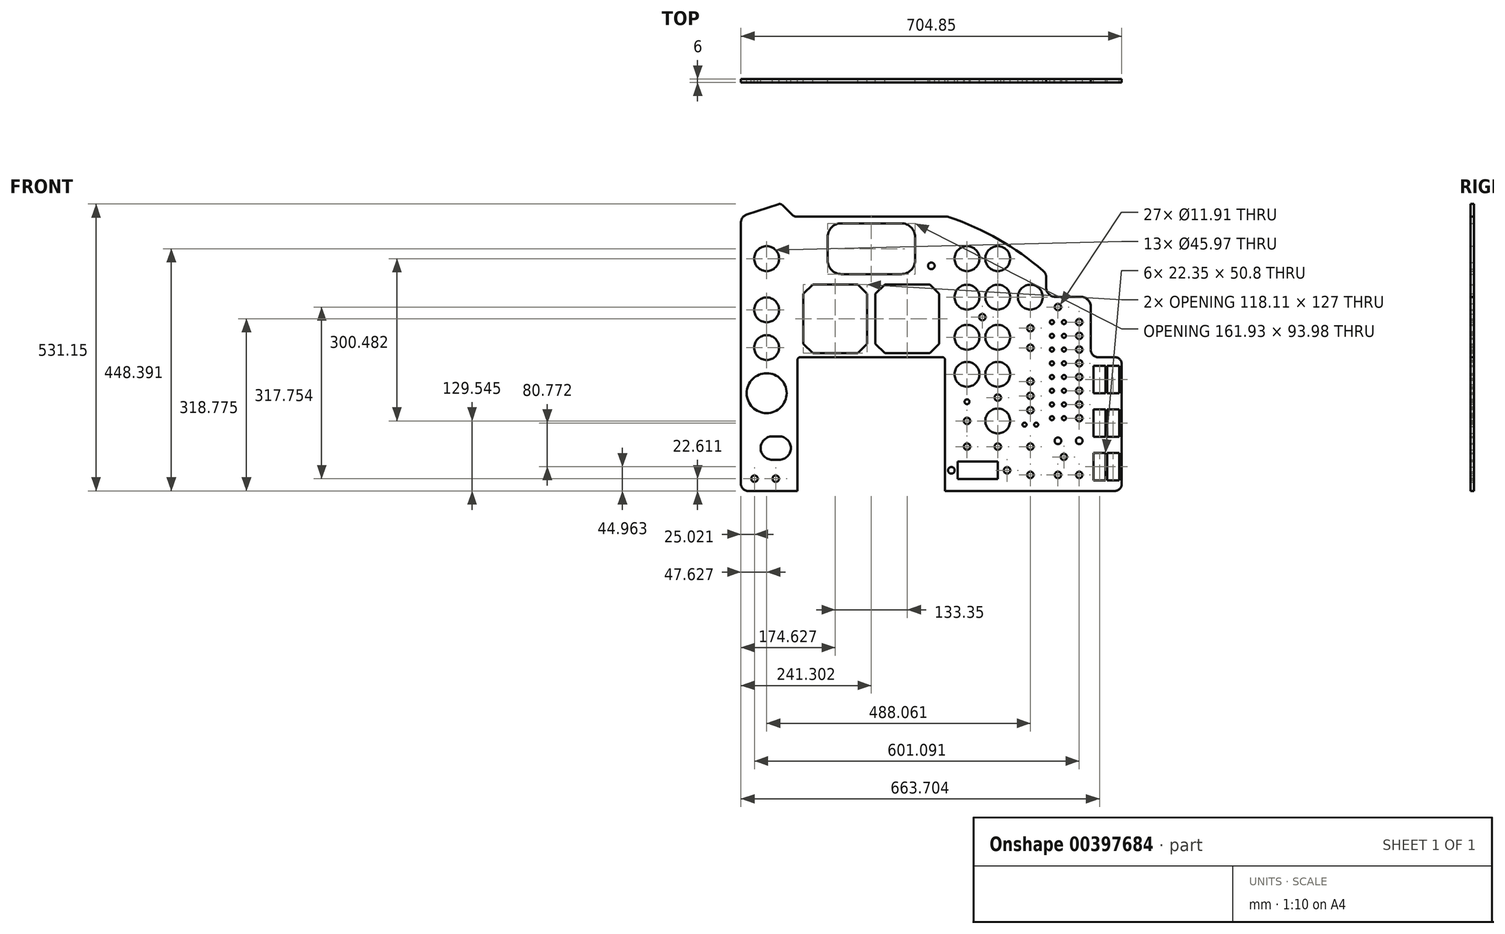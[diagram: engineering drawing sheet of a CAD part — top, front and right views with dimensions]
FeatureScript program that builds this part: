
annotation { "Feature Type Name" : "Feature", "Feature Type Description" : "" }
export const myFeature = defineFeature(function(context is Context, id is Id, definition is map)
    precondition{}
    {
        {
            var Q0;
            Q0=qCreatedBy(makeId("Front.planeOp"),FACE);
            var sketch = newSketch(context, id + "F0", { "sketchPlane" : qUnion([Q0])});
            skLineSegment(sketch, "E0", {"start": v(-241.06, -131.64) * mm, "end": v(-148.98, -131.64) * mm});
            skLineSegment(sketch, "E1", {"start": v(-148.98, -131.64) * mm, "end": v(-148.98, 110.93) * mm});
            skLineSegment(sketch, "E2", {"start": v(-143.9, 116.01) * mm, "end": v(118.99, 116.01) * mm});
            skLineSegment(sketch, "E3", {"start": v(124.07, 110.93) * mm, "end": v(124.07, -131.64) * mm});
            skLineSegment(sketch, "E4", {"start": v(124.07, -131.64) * mm, "end": v(311.4, -131.64) * mm});
            skLineSegment(sketch, "E5", {"start": v(-253.76, 255.71) * mm, "end": v(-253.76, -118.94) * mm});
            skLineSegment(sketch, "E6", {"start": v(-152.74, 376.44) * mm, "end": v(117.72, 376.44) * mm});
            skLineSegment(sketch, "E7", {"start": v(-253.76, 255.71) * mm, "end": v(-253.76, 365.39) * mm});
            skLineSegment(sketch, "E8", {"start": v(311.4, -131.64) * mm, "end": v(438.4, -131.64) * mm});
            skLineSegment(sketch, "E9", {"start": v(451.1, -118.94) * mm, "end": v(451.1, 103.31) * mm});
            skLineSegment(sketch, "E10", {"start": v(438.4, 116.01) * mm, "end": v(406.64, 116.01) * mm});
            skLineSegment(sketch, "E11", {"start": v(393.94, 128.71) * mm, "end": v(393.94, 208.72) * mm});
            skLineSegment(sketch, "E12", {"start": v(374.9, 227.77) * mm, "end": v(327.9, 227.77) * mm});
            skLineSegment(sketch, "E13", {"start": v(-243.25, 379.87) * mm, "end": v(-184.35, 399.13) * mm});
            skLineSegment(sketch, "E14", {"start": v(-157.18, 378.26) * mm, "end": v(-176.65, 397.33) * mm});
            skLineSegment(sketch, "E15", {"start": v(117.72, 376.44) * mm, "end": v(123.7, 376.44) * mm});
            skLineSegment(sketch, "E16", {"start": v(311.4, 255.71) * mm, "end": v(311.4, 263.42) * mm});
            skLineSegment(sketch, "E17", {"start": v(-253.76, 376.44) * mm, "end": v(-155.33, 376.44) * mm, "construction": true});
            skLineSegment(sketch, "E18", {"start": v(-179.95, 400.57) * mm, "end": v(-179.95, 376.44) * mm, "construction": true});
            skLineSegment(sketch, "E19", {"start": v(217.5, 323.68) * mm, "end": v(223.32, 333.8) * mm, "construction": true});
            skArc(sketch, "E20", {"start": v(305.6, 275.97) * mm, "mid": v(223.45, 333.73) * mm, "end": v(131.93, 375.07) * mm});
            skLineSegment(sketch, "E21", {"start": v(127.88, 376.44) * mm, "end": v(311.4, 270.95) * mm, "construction": true});
            skPoint(sketch, "E22.visualSharp", {"position": v(451.1, -131.64) * mm});
            skArc(sketch, "E22.filletArc", {"start": v(438.4, -131.64) * mm, "mid": v(447.37, -127.92) * mm, "end": v(451.1, -118.94) * mm});
            skPoint(sketch, "E23.visualSharp", {"position": v(451.1, 116.01) * mm});
            skArc(sketch, "E23.filletArc", {"start": v(451.1, 103.31) * mm, "mid": v(447.37, 112.3) * mm, "end": v(438.4, 116.01) * mm});
            skPoint(sketch, "E24.visualSharp", {"position": v(393.94, 116.01) * mm});
            skArc(sketch, "E24.filletArc", {"start": v(393.94, 128.71) * mm, "mid": v(397.66, 119.73) * mm, "end": v(406.64, 116.01) * mm});
            skPoint(sketch, "E25.visualSharp", {"position": v(393.94, 227.77) * mm});
            skArc(sketch, "E25.filletArc", {"start": v(393.94, 208.72) * mm, "mid": v(388.36, 222.2) * mm, "end": v(374.9, 227.77) * mm});
            skPoint(sketch, "E26.visualSharp", {"position": v(124.07, 116.01) * mm});
            skArc(sketch, "E26.filletArc", {"start": v(124.07, 110.93) * mm, "mid": v(122.58, 114.53) * mm, "end": v(118.99, 116.01) * mm});
            skPoint(sketch, "E27.visualSharp", {"position": v(-148.98, 116.01) * mm});
            skArc(sketch, "E27.filletArc", {"start": v(-143.9, 116.01) * mm, "mid": v(-147.5, 114.53) * mm, "end": v(-148.98, 110.93) * mm});
            skPoint(sketch, "E28.visualSharp", {"position": v(-253.76, -131.64) * mm});
            skArc(sketch, "E28.filletArc", {"start": v(-253.76, -118.94) * mm, "mid": v(-250.04, -127.92) * mm, "end": v(-241.06, -131.64) * mm});
            skPoint(sketch, "E29.visualSharp", {"position": v(-155.33, 376.44) * mm});
            skArc(sketch, "E29.filletArc", {"start": v(-157.18, 378.26) * mm, "mid": v(-155.14, 376.91) * mm, "end": v(-152.74, 376.44) * mm});
            skPoint(sketch, "E30.visualSharp", {"position": v(-179.95, 400.57) * mm});
            skArc(sketch, "E30.filletArc", {"start": v(-176.65, 397.33) * mm, "mid": v(-180.25, 399.31) * mm, "end": v(-184.35, 399.13) * mm});
            skPoint(sketch, "E31.visualSharp", {"position": v(-253.76, 376.44) * mm});
            skArc(sketch, "E31.filletArc", {"start": v(-243.25, 379.87) * mm, "mid": v(-250.86, 374.34) * mm, "end": v(-253.76, 365.39) * mm});
            skLineSegment(sketch, "E32", {"start": v(311.4, 255.71) * mm, "end": v(311.4, 244.28) * mm});
            skPoint(sketch, "E33.visualSharp", {"position": v(311.4, 227.77) * mm});
            skArc(sketch, "E33.filletArc", {"start": v(311.4, 244.28) * mm, "mid": v(316.23, 232.61) * mm, "end": v(327.9, 227.77) * mm});
            skPoint(sketch, "E34.visualSharp", {"position": v(311.4, 270.95) * mm});
            skArc(sketch, "E34.filletArc", {"start": v(311.4, 263.42) * mm, "mid": v(309.88, 270.33) * mm, "end": v(305.6, 275.97) * mm});
            skPoint(sketch, "E35.visualSharp", {"position": v(127.88, 376.44) * mm});
            skArc(sketch, "E35.filletArc", {"start": v(131.93, 375.07) * mm, "mid": v(127.87, 376.1) * mm, "end": v(123.7, 376.44) * mm});
            skLineSegment(sketch, "E36", {"start": v(-206.13, -131.64) * mm, "end": v(-206.13, 376.44) * mm, "construction": true});
            skCircle(sketch, "E37", {"center": v(-206.13, 49.34) * mm, "radius": 36.96 * mm});
            skCircle(sketch, "E38", {"center": v(-206.13, 133.67) * mm, "radius": 22.99 * mm});
            skCircle(sketch, "E39", {"center": v(-206.13, 203.52) * mm, "radius": 22.99 * mm});
            skCircle(sketch, "E40", {"center": v(-206.13, 298.39) * mm, "radius": 22.99 * mm});
            skLineSegment(sketch, "E41", {"start": v(164.7, -131.64) * mm, "end": v(164.7, 355.27) * mm, "construction": true});
            skLineSegment(sketch, "E42", {"start": v(221.6, -131.64) * mm, "end": v(221.6, 322.57) * mm, "construction": true});
            skLineSegment(sketch, "E43", {"start": v(281.93, -131.64) * mm, "end": v(281.93, 287.9) * mm, "construction": true});
            skCircle(sketch, "E44", {"center": v(164.7, 84.26) * mm, "radius": 22.99 * mm});
            skCircle(sketch, "E45", {"center": v(164.7, 152.84) * mm, "radius": 22.99 * mm});
            skCircle(sketch, "E46", {"center": v(221.6, 152.84) * mm, "radius": 22.99 * mm});
            skCircle(sketch, "E47", {"center": v(221.6, 84.26) * mm, "radius": 22.99 * mm});
            skCircle(sketch, "E48", {"center": v(164.7, 227.14) * mm, "radius": 22.99 * mm});
            skCircle(sketch, "E49", {"center": v(221.6, 227.14) * mm, "radius": 22.99 * mm});
            skCircle(sketch, "E50", {"center": v(164.7, 298.39) * mm, "radius": 22.99 * mm});
            skCircle(sketch, "E51", {"center": v(221.6, 298.39) * mm, "radius": 22.99 * mm});
            skCircle(sketch, "E52", {"center": v(281.93, 227.14) * mm, "radius": 22.99 * mm});
            skLineSegment(sketch, "E53", {"start": v(372.35, -131.64) * mm, "end": v(372.35, 227.77) * mm, "construction": true});
            skLineSegment(sketch, "E54", {"start": v(332.98, -131.64) * mm, "end": v(332.98, 227.77) * mm, "construction": true});
            skLineSegment(sketch, "E55", {"start": v(435.34, -131.64) * mm, "end": v(435.34, 116.01) * mm, "construction": true});
            skLineSegment(sketch, "E56", {"start": v(409.94, -131.64) * mm, "end": v(409.94, 116.01) * mm, "construction": true});
            skCircle(sketch, "E57", {"center": v(372.35, 2.98) * mm, "radius": 5.95 * mm});
            skCircle(sketch, "E58.0.1.0", {"center": v(372.35, 28.38) * mm, "radius": 5.95 * mm});
            skCircle(sketch, "E58.0.2.0", {"center": v(372.35, 53.78) * mm, "radius": 5.95 * mm});
            skCircle(sketch, "E58.0.3.0", {"center": v(372.35, 79.18) * mm, "radius": 5.95 * mm});
            skCircle(sketch, "E58.0.4.0", {"center": v(372.35, 104.58) * mm, "radius": 5.95 * mm});
            skCircle(sketch, "E58.0.5.0", {"center": v(372.35, 129.98) * mm, "radius": 5.95 * mm});
            skCircle(sketch, "E58.0.6.0", {"center": v(372.35, 155.38) * mm, "radius": 5.95 * mm});
            skCircle(sketch, "E58.0.7.0", {"center": v(372.35, 180.78) * mm, "radius": 5.95 * mm});
            skLineSegment(sketch, "E58.direction1", {"start": v(372.35, 2.98) * mm, "end": v(397.75, 2.98) * mm, "construction": true});
            skLineSegment(sketch, "E58.direction2", {"start": v(372.35, 2.98) * mm, "end": v(372.35, 28.38) * mm, "construction": true});
            skCircle(sketch, "E59", {"center": v(321.8, 2.98) * mm, "radius": 3.77 * mm});
            skCircle(sketch, "E60.0.1.0", {"center": v(321.8, 28.38) * mm, "radius": 3.77 * mm});
            skCircle(sketch, "E60.0.2.0", {"center": v(321.8, 53.78) * mm, "radius": 3.77 * mm});
            skCircle(sketch, "E60.0.3.0", {"center": v(321.8, 79.18) * mm, "radius": 3.77 * mm});
            skCircle(sketch, "E60.0.4.0", {"center": v(321.8, 104.58) * mm, "radius": 3.77 * mm});
            skCircle(sketch, "E60.0.5.0", {"center": v(321.8, 129.98) * mm, "radius": 3.77 * mm});
            skCircle(sketch, "E60.0.6.0", {"center": v(321.8, 155.38) * mm, "radius": 3.77 * mm});
            skCircle(sketch, "E60.0.7.0", {"center": v(321.8, 180.78) * mm, "radius": 3.77 * mm});
            skCircle(sketch, "E60.1.0.0", {"center": v(344.16, 2.98) * mm, "radius": 3.77 * mm});
            skCircle(sketch, "E60.1.1.0", {"center": v(344.16, 28.38) * mm, "radius": 3.77 * mm});
            skCircle(sketch, "E60.1.2.0", {"center": v(344.16, 53.78) * mm, "radius": 3.77 * mm});
            skCircle(sketch, "E60.1.3.0", {"center": v(344.16, 79.18) * mm, "radius": 3.77 * mm});
            skCircle(sketch, "E60.1.4.0", {"center": v(344.16, 104.58) * mm, "radius": 3.77 * mm});
            skCircle(sketch, "E60.1.5.0", {"center": v(344.16, 129.98) * mm, "radius": 3.77 * mm});
            skCircle(sketch, "E60.1.6.0", {"center": v(344.16, 155.38) * mm, "radius": 3.77 * mm});
            skCircle(sketch, "E60.1.7.0", {"center": v(344.16, 180.78) * mm, "radius": 3.77 * mm});
            skLineSegment(sketch, "E60.direction1", {"start": v(321.8, 2.98) * mm, "end": v(344.16, 2.98) * mm, "construction": true});
            skLineSegment(sketch, "E60.direction2", {"start": v(321.8, 2.98) * mm, "end": v(321.8, 28.38) * mm, "construction": true});
            skLineSegment(sketch, "E61.bottom", {"start": v(-68.02, 363.74) * mm, "end": v(43.1, 363.74) * mm});
            skLineSegment(sketch, "E61.top", {"start": v(-68.02, 269.76) * mm, "end": v(43.1, 269.76) * mm});
            skLineSegment(sketch, "E61.left", {"start": v(-93.42, 338.34) * mm, "end": v(-93.42, 295.16) * mm});
            skLineSegment(sketch, "E61.right", {"start": v(68.5, 338.34) * mm, "end": v(68.5, 295.16) * mm});
            skLineSegment(sketch, "E62", {"start": v(-12.46, 116.01) * mm, "end": v(-12.46, 376.44) * mm, "construction": true});
            skPoint(sketch, "E63.visualSharp", {"position": v(-93.42, 363.74) * mm});
            skArc(sketch, "E63.filletArc", {"start": v(-68.02, 363.74) * mm, "mid": v(-85.98, 356.3) * mm, "end": v(-93.42, 338.34) * mm});
            skPoint(sketch, "E64.visualSharp", {"position": v(-93.42, 269.76) * mm});
            skArc(sketch, "E64.filletArc", {"start": v(-93.42, 295.16) * mm, "mid": v(-85.98, 277.2) * mm, "end": v(-68.02, 269.76) * mm});
            skPoint(sketch, "E65.visualSharp", {"position": v(68.5, 363.74) * mm});
            skArc(sketch, "E65.filletArc", {"start": v(68.5, 338.34) * mm, "mid": v(61.07, 356.3) * mm, "end": v(43.1, 363.74) * mm});
            skPoint(sketch, "E66.visualSharp", {"position": v(68.5, 269.76) * mm});
            skArc(sketch, "E66.filletArc", {"start": v(43.1, 269.76) * mm, "mid": v(61.07, 277.2) * mm, "end": v(68.5, 295.16) * mm});
            skLineSegment(sketch, "E67", {"start": v(113.27, 123.63) * mm, "end": v(96, 123.63) * mm, "construction": true});
            skLineSegment(sketch, "E68", {"start": v(113.27, 123.63) * mm, "end": v(113.27, 140.9) * mm, "construction": true});
            skLineSegment(sketch, "E69", {"start": v(113.27, 250.63) * mm, "end": v(113.27, 233.36) * mm, "construction": true});
            skLineSegment(sketch, "E70", {"start": v(113.27, 250.63) * mm, "end": v(96, 250.63) * mm, "construction": true});
            skLineSegment(sketch, "E71", {"start": v(-4.84, 250.63) * mm, "end": v(12.43, 250.63) * mm, "construction": true});
            skLineSegment(sketch, "E72", {"start": v(-4.84, 250.63) * mm, "end": v(-4.84, 233.36) * mm, "construction": true});
            skLineSegment(sketch, "E73", {"start": v(-4.84, 123.63) * mm, "end": v(-4.84, 140.9) * mm, "construction": true});
            skLineSegment(sketch, "E74", {"start": v(-4.84, 123.63) * mm, "end": v(12.43, 123.63) * mm, "construction": true});
            skLineSegment(sketch, "E75", {"start": v(12.43, 123.63) * mm, "end": v(96, 123.63) * mm});
            skLineSegment(sketch, "E76", {"start": v(113.27, 140.9) * mm, "end": v(96, 123.63) * mm});
            skLineSegment(sketch, "E77", {"start": v(113.27, 233.36) * mm, "end": v(113.27, 140.9) * mm});
            skLineSegment(sketch, "E78", {"start": v(113.27, 233.36) * mm, "end": v(96, 250.63) * mm});
            skLineSegment(sketch, "E79", {"start": v(96, 250.63) * mm, "end": v(12.43, 250.63) * mm});
            skLineSegment(sketch, "E80", {"start": v(-4.84, 233.36) * mm, "end": v(-4.84, 140.9) * mm});
            skLineSegment(sketch, "E81", {"start": v(-4.84, 140.9) * mm, "end": v(12.43, 123.63) * mm});
            skLineSegment(sketch, "E82", {"start": v(-4.84, 233.36) * mm, "end": v(12.43, 250.63) * mm});
            skLineSegment(sketch, "E83", {"start": v(-20.08, 123.63) * mm, "end": v(-37.35, 123.63) * mm, "construction": true});
            skLineSegment(sketch, "E84", {"start": v(-20.08, 123.63) * mm, "end": v(-20.08, 140.9) * mm, "construction": true});
            skLineSegment(sketch, "E85", {"start": v(-20.08, 250.63) * mm, "end": v(-20.08, 233.36) * mm, "construction": true});
            skLineSegment(sketch, "E86", {"start": v(-20.08, 250.63) * mm, "end": v(-37.35, 250.63) * mm, "construction": true});
            skLineSegment(sketch, "E87", {"start": v(-138.19, 250.63) * mm, "end": v(-120.92, 250.63) * mm, "construction": true});
            skLineSegment(sketch, "E88", {"start": v(-138.19, 250.63) * mm, "end": v(-138.19, 233.36) * mm, "construction": true});
            skLineSegment(sketch, "E89", {"start": v(-138.19, 123.63) * mm, "end": v(-138.19, 140.9) * mm, "construction": true});
            skLineSegment(sketch, "E90", {"start": v(-138.19, 123.63) * mm, "end": v(-120.92, 123.63) * mm, "construction": true});
            skLineSegment(sketch, "E91", {"start": v(-120.92, 123.63) * mm, "end": v(-37.35, 123.63) * mm});
            skLineSegment(sketch, "E92", {"start": v(-20.08, 140.9) * mm, "end": v(-37.35, 123.63) * mm});
            skLineSegment(sketch, "E93", {"start": v(-20.08, 233.36) * mm, "end": v(-20.08, 140.9) * mm});
            skLineSegment(sketch, "E94", {"start": v(-20.08, 233.36) * mm, "end": v(-37.35, 250.63) * mm});
            skLineSegment(sketch, "E95", {"start": v(-37.35, 250.63) * mm, "end": v(-120.92, 250.63) * mm});
            skLineSegment(sketch, "E96", {"start": v(-138.19, 233.36) * mm, "end": v(-138.19, 140.9) * mm});
            skLineSegment(sketch, "E97", {"start": v(-138.19, 140.9) * mm, "end": v(-120.92, 123.63) * mm});
            skLineSegment(sketch, "E98", {"start": v(-138.19, 233.36) * mm, "end": v(-120.92, 250.63) * mm});
            skLineSegment(sketch, "E99.bottom", {"start": v(354.57, 13.97) * mm, "end": v(311.4, 13.97) * mm, "construction": true});
            skLineSegment(sketch, "E99.top", {"start": v(354.57, -8) * mm, "end": v(311.4, -8) * mm, "construction": true});
            skLineSegment(sketch, "E99.left", {"start": v(354.57, 13.97) * mm, "end": v(354.57, -8) * mm, "construction": true});
            skLineSegment(sketch, "E99.right", {"start": v(311.4, 13.97) * mm, "end": v(311.4, -8) * mm, "construction": true});
            skPoint(sketch, "E99.middle", {"position": v(332.98, 2.98) * mm});
            skLineSegment(sketch, "E100.0.1.0", {"start": v(354.57, 39.37) * mm, "end": v(311.4, 39.37) * mm, "construction": true});
            skLineSegment(sketch, "E100.0.1.1", {"start": v(354.57, 39.37) * mm, "end": v(354.57, 17.4) * mm, "construction": true});
            skLineSegment(sketch, "E100.0.1.2", {"start": v(354.57, 17.4) * mm, "end": v(311.4, 17.4) * mm, "construction": true});
            skLineSegment(sketch, "E100.0.1.3", {"start": v(311.4, 39.37) * mm, "end": v(311.4, 17.4) * mm, "construction": true});
            skLineSegment(sketch, "E100.0.2.0", {"start": v(354.57, 64.77) * mm, "end": v(311.4, 64.77) * mm, "construction": true});
            skLineSegment(sketch, "E100.0.2.1", {"start": v(354.57, 64.77) * mm, "end": v(354.57, 42.8) * mm, "construction": true});
            skLineSegment(sketch, "E100.0.2.2", {"start": v(354.57, 42.8) * mm, "end": v(311.4, 42.8) * mm, "construction": true});
            skLineSegment(sketch, "E100.0.2.3", {"start": v(311.4, 64.77) * mm, "end": v(311.4, 42.8) * mm, "construction": true});
            skLineSegment(sketch, "E100.0.3.0", {"start": v(354.57, 90.17) * mm, "end": v(311.4, 90.17) * mm, "construction": true});
            skLineSegment(sketch, "E100.0.3.1", {"start": v(354.57, 90.17) * mm, "end": v(354.57, 68.2) * mm, "construction": true});
            skLineSegment(sketch, "E100.0.3.2", {"start": v(354.57, 68.2) * mm, "end": v(311.4, 68.2) * mm, "construction": true});
            skLineSegment(sketch, "E100.0.3.3", {"start": v(311.4, 90.17) * mm, "end": v(311.4, 68.2) * mm, "construction": true});
            skLineSegment(sketch, "E100.0.4.0", {"start": v(354.57, 115.57) * mm, "end": v(311.4, 115.57) * mm, "construction": true});
            skLineSegment(sketch, "E100.0.4.1", {"start": v(354.57, 115.57) * mm, "end": v(354.57, 93.6) * mm, "construction": true});
            skLineSegment(sketch, "E100.0.4.2", {"start": v(354.57, 93.6) * mm, "end": v(311.4, 93.6) * mm, "construction": true});
            skLineSegment(sketch, "E100.0.4.3", {"start": v(311.4, 115.57) * mm, "end": v(311.4, 93.6) * mm, "construction": true});
            skLineSegment(sketch, "E100.0.5.0", {"start": v(354.57, 140.97) * mm, "end": v(311.4, 140.97) * mm, "construction": true});
            skLineSegment(sketch, "E100.0.5.1", {"start": v(354.57, 140.97) * mm, "end": v(354.57, 119) * mm, "construction": true});
            skLineSegment(sketch, "E100.0.5.2", {"start": v(354.57, 119) * mm, "end": v(311.4, 119) * mm, "construction": true});
            skLineSegment(sketch, "E100.0.5.3", {"start": v(311.4, 140.97) * mm, "end": v(311.4, 119) * mm, "construction": true});
            skLineSegment(sketch, "E100.0.6.0", {"start": v(354.57, 166.37) * mm, "end": v(311.4, 166.37) * mm, "construction": true});
            skLineSegment(sketch, "E100.0.6.1", {"start": v(354.57, 166.37) * mm, "end": v(354.57, 144.4) * mm, "construction": true});
            skLineSegment(sketch, "E100.0.6.2", {"start": v(354.57, 144.4) * mm, "end": v(311.4, 144.4) * mm, "construction": true});
            skLineSegment(sketch, "E100.0.6.3", {"start": v(311.4, 166.37) * mm, "end": v(311.4, 144.4) * mm, "construction": true});
            skLineSegment(sketch, "E100.0.7.0", {"start": v(354.57, 191.77) * mm, "end": v(311.4, 191.77) * mm, "construction": true});
            skLineSegment(sketch, "E100.0.7.1", {"start": v(354.57, 191.77) * mm, "end": v(354.57, 169.8) * mm, "construction": true});
            skLineSegment(sketch, "E100.0.7.2", {"start": v(354.57, 169.8) * mm, "end": v(311.4, 169.8) * mm, "construction": true});
            skLineSegment(sketch, "E100.0.7.3", {"start": v(311.4, 191.77) * mm, "end": v(311.4, 169.8) * mm, "construction": true});
            skLineSegment(sketch, "E100.direction1", {"start": v(311.4, -8) * mm, "end": v(336.8, -8) * mm, "construction": true});
            skLineSegment(sketch, "E100.direction2", {"start": v(311.4, -8) * mm, "end": v(311.4, 17.4) * mm, "construction": true});
            skLineSegment(sketch, "E101.bottom", {"start": v(421.12, -112.08) * mm, "end": v(398.77, -112.08) * mm});
            skLineSegment(sketch, "E101.top", {"start": v(421.12, -61.28) * mm, "end": v(398.77, -61.28) * mm});
            skLineSegment(sketch, "E101.left", {"start": v(421.12, -112.08) * mm, "end": v(421.12, -61.28) * mm});
            skLineSegment(sketch, "E101.right", {"start": v(398.77, -112.08) * mm, "end": v(398.77, -61.28) * mm});
            skPoint(sketch, "E101.middle", {"position": v(409.94, -86.68) * mm});
            skPoint(sketch, "E102.0.1.0", {"position": v(409.94, -5.9) * mm});
            skLineSegment(sketch, "E102.0.1.1", {"start": v(421.12, -31.3) * mm, "end": v(421.12, 19.5) * mm});
            skLineSegment(sketch, "E102.0.1.2", {"start": v(398.77, -31.3) * mm, "end": v(398.77, 19.5) * mm});
            skLineSegment(sketch, "E102.0.1.3", {"start": v(421.12, 19.5) * mm, "end": v(398.77, 19.5) * mm});
            skLineSegment(sketch, "E102.0.1.4", {"start": v(421.12, -31.3) * mm, "end": v(398.77, -31.3) * mm});
            skPoint(sketch, "E102.0.2.0", {"position": v(409.94, 74.87) * mm});
            skLineSegment(sketch, "E102.0.2.1", {"start": v(421.12, 49.47) * mm, "end": v(421.12, 100.27) * mm});
            skLineSegment(sketch, "E102.0.2.2", {"start": v(398.77, 49.47) * mm, "end": v(398.77, 100.27) * mm});
            skLineSegment(sketch, "E102.0.2.3", {"start": v(421.12, 100.27) * mm, "end": v(398.77, 100.27) * mm});
            skLineSegment(sketch, "E102.0.2.4", {"start": v(421.12, 49.47) * mm, "end": v(398.77, 49.47) * mm});
            skPoint(sketch, "E102.1.0.0", {"position": v(435.34, -86.68) * mm});
            skLineSegment(sketch, "E102.1.0.1", {"start": v(446.52, -112.08) * mm, "end": v(446.52, -61.28) * mm});
            skLineSegment(sketch, "E102.1.0.2", {"start": v(424.17, -112.08) * mm, "end": v(424.17, -61.28) * mm});
            skLineSegment(sketch, "E102.1.0.3", {"start": v(446.52, -61.28) * mm, "end": v(424.17, -61.28) * mm});
            skLineSegment(sketch, "E102.1.0.4", {"start": v(446.52, -112.08) * mm, "end": v(424.17, -112.08) * mm});
            skPoint(sketch, "E102.1.1.0", {"position": v(435.34, -5.9) * mm});
            skLineSegment(sketch, "E102.1.1.1", {"start": v(446.52, -31.3) * mm, "end": v(446.52, 19.5) * mm});
            skLineSegment(sketch, "E102.1.1.2", {"start": v(424.17, -31.3) * mm, "end": v(424.17, 19.5) * mm});
            skLineSegment(sketch, "E102.1.1.3", {"start": v(446.52, 19.5) * mm, "end": v(424.17, 19.5) * mm});
            skLineSegment(sketch, "E102.1.1.4", {"start": v(446.52, -31.3) * mm, "end": v(424.17, -31.3) * mm});
            skPoint(sketch, "E102.1.2.0", {"position": v(435.34, 74.87) * mm});
            skLineSegment(sketch, "E102.1.2.1", {"start": v(446.52, 49.47) * mm, "end": v(446.52, 100.27) * mm});
            skLineSegment(sketch, "E102.1.2.2", {"start": v(424.17, 49.47) * mm, "end": v(424.17, 100.27) * mm});
            skLineSegment(sketch, "E102.1.2.3", {"start": v(446.52, 100.27) * mm, "end": v(424.17, 100.27) * mm});
            skLineSegment(sketch, "E102.1.2.4", {"start": v(446.52, 49.47) * mm, "end": v(424.17, 49.47) * mm});
            skLineSegment(sketch, "E102.direction1", {"start": v(398.77, -112.08) * mm, "end": v(424.17, -112.08) * mm, "construction": true});
            skLineSegment(sketch, "E102.direction2", {"start": v(398.77, -112.08) * mm, "end": v(398.77, -31.3) * mm, "construction": true});
            skCircle(sketch, "E103", {"center": v(-189.37, -109.03) * mm, "radius": 5.95 * mm});
            skCircle(sketch, "E104", {"center": v(-228.74, -109.03) * mm, "radius": 5.95 * mm});
            skLineSegment(sketch, "E105", {"start": v(-148.98, -109.03) * mm, "end": v(-253.76, -109.03) * mm, "construction": true});
            skLineSegment(sketch, "E106", {"start": v(124.07, 84.26) * mm, "end": v(281.93, 84.26) * mm, "construction": true});
            skLineSegment(sketch, "E107", {"start": v(281.93, 152.84) * mm, "end": v(125.15, 152.84) * mm, "construction": true});
            skLineSegment(sketch, "E108", {"start": v(281.93, 227.14) * mm, "end": v(116.2, 227.14) * mm, "construction": true});
            skCircle(sketch, "E109", {"center": v(332.98, 208.72) * mm, "radius": 5.95 * mm});
            skLineSegment(sketch, "E110", {"start": v(281.93, -101.92) * mm, "end": v(451.1, -101.92) * mm, "construction": true});
            skCircle(sketch, "E111", {"center": v(281.93, -101.92) * mm, "radius": 5.95 * mm});
            skCircle(sketch, "E112", {"center": v(332.98, -101.92) * mm, "radius": 5.95 * mm});
            skCircle(sketch, "E113", {"center": v(372.35, -101.92) * mm, "radius": 5.95 * mm});
            skLineSegment(sketch, "E114", {"start": v(124.07, -49.6) * mm, "end": v(281.93, -49.6) * mm, "construction": true});
            skLineSegment(sketch, "E115", {"start": v(124.07, -93.54) * mm, "end": v(281.93, -93.54) * mm, "construction": true});
            skCircle(sketch, "E116", {"center": v(164.7, -49.6) * mm, "radius": 5.95 * mm});
            skCircle(sketch, "E117", {"center": v(281.93, -49.6) * mm, "radius": 5.95 * mm});
            skLineSegment(sketch, "E118.bottom", {"start": v(260.34, 2.03) * mm, "end": v(303.52, 2.03) * mm, "construction": true});
            skLineSegment(sketch, "E118.top", {"start": v(260.34, -19.94) * mm, "end": v(303.52, -19.94) * mm, "construction": true});
            skLineSegment(sketch, "E118.left", {"start": v(260.34, 2.03) * mm, "end": v(260.34, -19.94) * mm, "construction": true});
            skLineSegment(sketch, "E118.right", {"start": v(303.52, 2.03) * mm, "end": v(303.52, -19.94) * mm, "construction": true});
            skPoint(sketch, "E118.middle", {"position": v(281.93, -8.95) * mm});
            skLineSegment(sketch, "E119", {"start": v(281.93, -8.95) * mm, "end": v(303.52, -8.95) * mm, "construction": true});
            skLineSegment(sketch, "E120", {"start": v(281.93, -8.95) * mm, "end": v(260.34, -8.95) * mm, "construction": true});
            skCircle(sketch, "E121", {"center": v(271.13, -8.95) * mm, "radius": 3.77 * mm});
            skCircle(sketch, "E122", {"center": v(292.72, -8.95) * mm, "radius": 3.77 * mm});
            skCircle(sketch, "E123", {"center": v(281.93, 17.72) * mm, "radius": 5.95 * mm});
            skCircle(sketch, "E124", {"center": v(281.93, 44.39) * mm, "radius": 5.95 * mm});
            skCircle(sketch, "E125", {"center": v(281.93, 71.06) * mm, "radius": 5.95 * mm});
            skLineSegment(sketch, "E126", {"start": v(451.1, -38.93) * mm, "end": v(281.93, -38.93) * mm, "construction": true});
            skLineSegment(sketch, "E127", {"start": v(164.7, 190) * mm, "end": v(221.6, 190) * mm, "construction": true});
            skLineSegment(sketch, "E128", {"start": v(164.7, 227.14) * mm, "end": v(164.7, 152.84) * mm, "construction": true});
            skCircle(sketch, "E129", {"center": v(193.16, 190) * mm, "radius": 5.95 * mm});
            skCircle(sketch, "E130", {"center": v(281.93, 169.6) * mm, "radius": 5.95 * mm});
            skCircle(sketch, "E131", {"center": v(281.93, 133.29) * mm, "radius": 5.95 * mm});
            skCircle(sketch, "E132", {"center": v(221.6, 41.08) * mm, "radius": 5.95 * mm});
            skLineSegment(sketch, "E133.bottom", {"start": v(221.6, -109.66) * mm, "end": v(147.44, -109.66) * mm});
            skLineSegment(sketch, "E133.top", {"start": v(221.6, -77.4) * mm, "end": v(147.44, -77.4) * mm});
            skLineSegment(sketch, "E133.left", {"start": v(221.6, -109.66) * mm, "end": v(221.6, -77.4) * mm});
            skLineSegment(sketch, "E133.right", {"start": v(147.44, -109.66) * mm, "end": v(147.44, -77.4) * mm});
            skPoint(sketch, "E133.middle", {"position": v(184.52, -93.54) * mm});
            skCircle(sketch, "E134", {"center": v(238.88, -93.54) * mm, "radius": 5.95 * mm});
            skCircle(sketch, "E135", {"center": v(135.75, -93.54) * mm, "radius": 6.15 * mm});
            skCircle(sketch, "E136", {"center": v(343.9, -68.64) * mm, "radius": 5.95 * mm});
            skCircle(sketch, "E137", {"center": v(221.6, -49.6) * mm, "radius": 5.95 * mm});
            skCircle(sketch, "E138", {"center": v(332.98, -38.93) * mm, "radius": 6.15 * mm});
            skCircle(sketch, "E139", {"center": v(372.35, -38.93) * mm, "radius": 6.15 * mm});
            skCircle(sketch, "E140", {"center": v(98.67, 285) * mm, "radius": 6.15 * mm});
            skLineSegment(sketch, "E141", {"start": v(124.07, -2.1) * mm, "end": v(221.6, -2.1) * mm, "construction": true});
            skCircle(sketch, "E142", {"center": v(164.7, -2.1) * mm, "radius": 5.95 * mm});
            skCircle(sketch, "E143", {"center": v(221.6, -2.1) * mm, "radius": 22.99 * mm});
            skLineSegment(sketch, "E144", {"start": v(-253.76, -52.3) * mm, "end": v(-148.98, -52.3) * mm, "construction": true});
            skLineSegment(sketch, "E145", {"start": v(-189.37, -109.03) * mm, "end": v(-189.37, -8.69) * mm, "construction": true});
            skLineSegment(sketch, "E146.bottom", {"start": v(-195.72, -30.7) * mm, "end": v(-183.02, -30.7) * mm, "construction": true});
            skLineSegment(sketch, "E146.top", {"start": v(-195.72, -73.89) * mm, "end": v(-183.02, -73.89) * mm, "construction": true});
            skLineSegment(sketch, "E146.left", {"start": v(-195.72, -30.7) * mm, "end": v(-195.72, -73.89) * mm, "construction": true});
            skLineSegment(sketch, "E146.right", {"start": v(-183.02, -30.7) * mm, "end": v(-183.02, -73.89) * mm, "construction": true});
            skPoint(sketch, "E146.middle", {"position": v(-189.37, -52.3) * mm});
            skArc(sketch, "E147", {"start": v(-183.02, -30.7) * mm, "mid": v(-161.43, -52.3) * mm, "end": v(-183.02, -73.89) * mm});
            skArc(sketch, "E148", {"start": v(-195.72, -30.7) * mm, "mid": v(-217.3, -52.3) * mm, "end": v(-195.72, -73.89) * mm});
            skLineSegment(sketch, "E149", {"start": v(-195.72, -30.7) * mm, "end": v(-183.02, -30.7) * mm});
            skLineSegment(sketch, "E150", {"start": v(-195.72, -73.89) * mm, "end": v(-183.02, -73.89) * mm});
            skCircle(sketch, "E151", {"center": v(164.7, 33.46) * mm, "radius": 4.5 * mm});
            skLineSegment(sketch, "E152", {"start": v(311.4, 244.28) * mm, "end": v(311.4, -131.64) * mm, "construction": true});
            skLineSegment(sketch, "E153", {"start": v(311.4, 255.71) * mm, "end": v(-253.76, 255.71) * mm});
            skSolve(sketch);
        }
        {
            var Q0;
            Q0 = qSketchRegion(id + "F0", true);
            extrude(context, id + "F1", {"entities" : qUnion([Q0]), "depth" : 6 * mm});
        }
    });
